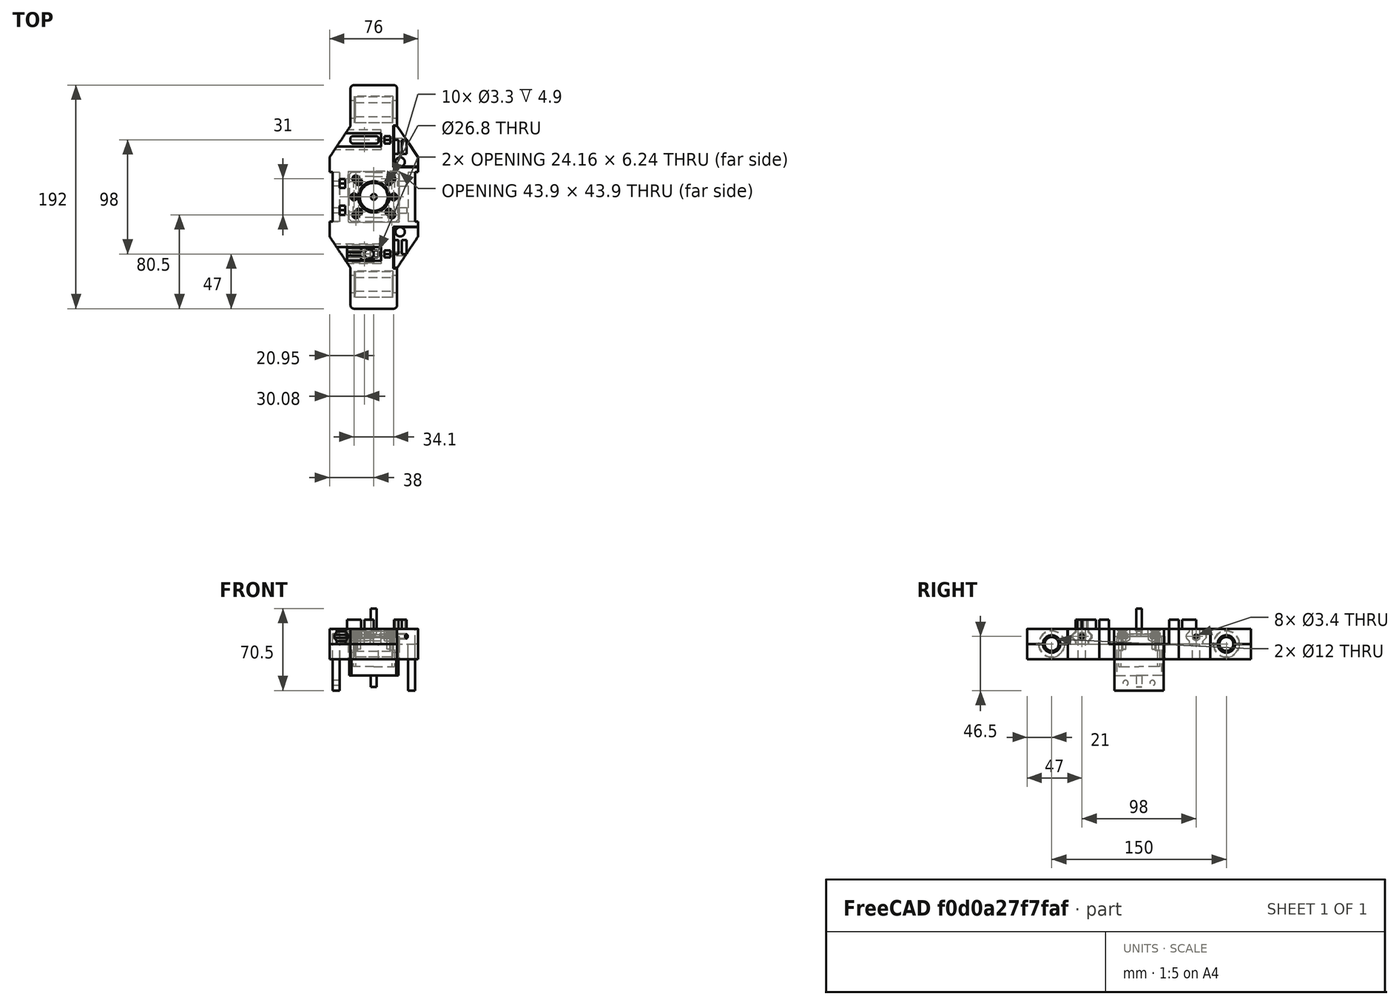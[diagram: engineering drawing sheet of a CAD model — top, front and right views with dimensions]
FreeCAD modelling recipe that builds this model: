
FCSTD DOCUMENT  (FreeCAD 0.16R6706 (Git))
Label: central_slider_v0
License: All rights reserved
LicenseURL: http://en.wikipedia.org/wiki/All_rights_reserved
objects: Part::Feature×19, Part::Cylinder×14, Part::FeaturePython×13, Part::MultiFuse×13, Part::Prism×10, Part::Extrusion×7, Part::Fuse×7, Part::Box×6, Part::Polygon×4, Part::Cut×4, Part::Circle×3, Part::Common×3, Part::Fillet×2
note: 105 computed .brp shape members not serialized (recipe doc carries the construction recipe); baked Part::Feature solids carry a one-line shape summary decoded from their .brp

FEATURE [Part::Polygon] topcenslid_box_sq
  Close = true
  Nodes = (4) [(-20,-96,0),(20,-96,0),(20,96,0),(-20,96,0)]
FEATURE [Part::Extrusion] topcenslid_box
  Base = -> topcenslid_box_sq
  Dir = (0,0,13)
  Solid = true
FEATURE [Part::Polygon] botcenslid_box_sq
  Close = true
  Nodes = (4) [(-20,-96,0),(20,-96,0),(20,96,0),(-20,96,0)]
FEATURE [Part::Extrusion] botcenslid_box
  Base = -> botcenslid_box_sq
  Dir = (0,0,13)
  Placement = pos=(0,0,-13) rot=(0,0,1;0rad)
  Solid = true
FEATURE [Part::Fillet] topcenslid_fllt
  Base = -> topcenslid_box
  Edges = 4 edges r=3: [Edge1,Edge2,Edge5,Edge8]
FEATURE [Part::Fillet] botcenslid_fllt
  Base = -> botcenslid_box
  Edges = 4 edges r=3: [Edge1,Edge2,Edge5,Edge8]
FEATURE [Part::Feature] topcenslidedent
  shape: bbox 76 x 125 x 13 mm, 14 faces (baked)
FEATURE [Part::Feature] botcenslidedent
  shape: bbox 76 x 125 x 13 mm, 14 faces (baked)
FEATURE [Part::Fuse] topcenslid_dent
  Base = -> topcenslid_fllt
  Tool = -> topcenslidedent
FEATURE [Part::Fuse] botcenslid_dent
  Base = -> botcenslid_fllt
  Tool = -> botcenslidedent
FEATURE [Part::Circle] toprod_circ
  Angle0 = 0
  Angle1 = 360
  Placement = pos=(-21,0,0) rot=(0,1,0;1.5708rad)
  Radius = 7.5
FEATURE [Part::Extrusion] toprod
  Base = -> toprod_circ
  Dir = (42,0,0)
  Placement = pos=(0,75,0) rot=(0,0,1;0rad)
  Solid = true
FEATURE [Part::Circle] botrod_circ
  Angle0 = 0
  Angle1 = 360
  Placement = pos=(-21,0,0) rot=(0,1,0;1.5708rad)
  Radius = 7.5
FEATURE [Part::Extrusion] botrod
  Base = -> botrod_circ
  Dir = (42,0,0)
  Placement = pos=(0,-75,0) rot=(0,0,1;0rad)
  Solid = true
FEATURE [Part::Feature] fbclt
  Placement = pos=(0,0,-0.1) rot=(0,0,1;0rad)
  shape: bbox 20.8 x 35 x 21 mm, 20 faces (baked)
FEATURE [Part::Feature] cbs_cfbclt
  shape: bbox 22.2 x 35.8 x 15 mm, 6 faces (baked)
FEATURE [Part::Feature] fbclb
  Placement = pos=(0,0,-0.2) rot=(0,0,1;0rad)
  shape: bbox 20.8 x 35 x 21 mm, 20 faces (baked)
FEATURE [Part::Feature] cbs_cfbclb
  shape: bbox 22.2 x 35.8 x 15 mm, 6 faces (baked)
FEATURE [Part::Cylinder] cen_lm12uu_0_ext
  Angle = 360
  Height = 32
  Placement = pos=(-16,0,0) rot=(0,1,0;1.5708rad)
  Radius = 11
FEATURE [Part::Cylinder] cen_lm12uu_0_int
  Angle = 360
  Height = 34
  Placement = pos=(-17,0,0) rot=(0,1,0;1.5708rad)
  Radius = 6
FEATURE [Part::Cut] cen_lm12uu_0
  Base = -> cen_lm12uu_0_ext
  Placement = pos=(0,75,0) rot=(0,0,1;0rad)
  Tool = -> cen_lm12uu_0_int
FEATURE [Part::Circle] cen_lm12uu_0_cont_circ
  Angle0 = 0
  Angle1 = 360
  Placement = pos=(-16.5,0,0) rot=(0,1,0;1.5708rad)
  Radius = 11.35
FEATURE [Part::Extrusion] cen_lm12uu_0_cont
  Base = -> cen_lm12uu_0_cont_circ
  Dir = (33,0,0)
  Placement = pos=(0,75,0) rot=(0,0,1;0rad)
  Solid = true
FEATURE [Part::FeaturePython] Clone  label="cen_lm12uu_001"  # Draft clone (typed FeaturePython)
  Objects = -> [cen_lm12uu_0]
  Placement = pos=(0,-75,0) rot=(0,0,1;0rad)
  Scale = (1,1,1)
FEATURE [Part::FeaturePython] Clone001  label="cen_lm12uu_0_cont001"  # Draft clone (typed FeaturePython)
  Objects = -> [cen_lm12uu_0_cont]
  Placement = pos=(0,-75,0) rot=(0,0,1;0rad)
  Scale = (1,1,1)
FEATURE [Part::Box] bclten0_cb1
  Height = 9
  Length = 12
  Placement = pos=(11,2.70833,12) rot=(0,0,1;0rad)
  Width = 4
FEATURE [Part::Box] bclten0_cb3
  Height = 9
  Length = 12
  Placement = pos=(11,9.50833,12) rot=(0,0,1;0rad)
  Width = 4
FEATURE [Part::Cylinder] bclten0_cyl
  Angle = 360
  Height = 9
  Placement = pos=(4,8.10833,12) rot=(0,0,1;0rad)
  Radius = 4
FEATURE [Part::Polygon] bclten0base_plane_yz
  Close = true
  Nodes = (12) [(0,2.90833,0),(0,2.90833,2.8375),(0,0.2,5.54583),(0,0.2,7.45417),(0,2.90833,10.1625),(0,2.90833,13),(0,13.3083,13),(0,13.3083,10.1625),+4 more]
FEATURE [Part::Extrusion] bclten0extr_base
  Base = -> bclten0base_plane_yz
  Dir = (23,0,0)
  Solid = true
FEATURE [Part::MultiFuse] bclten0clamp_base
  Shapes = -> [bclten0_cb1,bclten0_cb3,bclten0_cyl,bclten0extr_base]
FEATURE [Part::Polygon] bclten0_baseof_plane_yz
  Close = true
  Nodes = (12) [(0,2.30833,0),(0,2.30833,2.4375),(0,-0.4,5.14583),(0,-0.4,7.85417),(0,2.30833,10.5625),(0,2.30833,13),(0,13.9083,13),(0,13.9083,10.5625),+4 more]
FEATURE [Part::Extrusion] bclten0_baseof
  Base = -> bclten0_baseof_plane_yz
  Dir = (44.16,0,0)
  Placement = pos=(6.16,57.1083,0) rot=(0,0,1;3.14159rad)
  Solid = true
FEATURE [Part::Cylinder] bclten0_base_lscrew_shank
  Angle = 360
  Height = 25
  Placement = pos=(0,0,-1) rot=(0,0,1;0rad)
  Radius = 1.7
FEATURE [Part::Cylinder] bclten0_base_lscrew_head
  Angle = 360
  Height = 9.5
  Placement = pos=(0,0,-1) rot=(0,0,1;0rad)
  Radius = 2.95
FEATURE [Part::MultiFuse] bclten0_base_lscrew
  Placement = pos=(23,8.10833,6.5) rot=(0,-1,0;1.5708rad)
  Shapes = -> [bclten0_base_lscrew_shank,bclten0_base_lscrew_head]
FEATURE [Part::Prism] bclten0_base_lscrew_nut
  Circumradius = 3.605
  Height = 5.04
  Placement = pos=(3,8.10833,6.9) rot=(0,1,0;1.5708rad)
  Polygon = 6
FEATURE [Part::Box] bclten0_base_lscrew_nut2
  Height = 6.9
  Length = 5.04
  Placement = pos=(3,4.9864,0) rot=(0,0,1;0rad)
  Width = 6.24386
FEATURE [Part::MultiFuse] bclten0_clamp_hole
  Shapes = -> [bclten0_base_lscrew,bclten0_base_lscrew_nut,bclten0_base_lscrew_nut2]
FEATURE [Part::Cut] bclten0
  Base = -> bclten0clamp_base
  Placement = pos=(6.16,57.1083,0) rot=(0,0,1;3.14159rad)
  Tool = -> bclten0_clamp_hole
FEATURE [Part::Prism] bccr_nuthole0_nut
  Circumradius = 3.605
  Height = 5.04
  Placement = pos=(0,0,0) rot=(0,1,0;1.5708rad)
  Polygon = 6
FEATURE [Part::Box] bccr_nuthole0_hole
  Height = 7.9
  Length = 5.04
  Placement = pos=(0,-3.12193,0) rot=(0,0,1;0rad)
  Width = 6.24386
FEATURE [Part::Fuse] bccr_nuthole0
  Base = -> bccr_nuthole0_nut
  Placement = pos=(9.16,49,6.5) rot=(0,0,1;0rad)
  Tool = -> bccr_nuthole0_hole
FEATURE [Part::Feature] bcl_leads0
  shape: bbox 32.84 x 3.4 x 3.4 mm, 3 faces (baked)
FEATURE [Part::Feature] boxb0
  shape: bbox 24.16 x 6.244 x 15 mm, 10 faces (baked)
FEATURE [Part::MultiFuse] beltholes_t
  Shapes = -> [bccr_nuthole0,bclten0_baseof,bcl_leads0,boxb0]
FEATURE [Part::FeaturePython] Clone002  label="bclten1"  # Draft clone (typed FeaturePython)
  Objects = -> [bclten0]
  Placement = pos=(0,-40.8917,0) rot=(0,0,1;3.14159rad)
  Scale = (1,1,1)
FEATURE [Part::FeaturePython] Clone003  label="beltholes_b"  # Draft clone (typed FeaturePython)
  Objects = -> [beltholes_t]
  Placement = pos=(0,-98,0) rot=(0,0,1;0rad)
  Scale = (1,1,1)
FEATURE [Part::Cylinder] b2hole00_shank
  Angle = 360
  Height = 14
  Placement = pos=(0,0,-1) rot=(0,0,1;0rad)
  Radius = 1.65
FEATURE [Part::Cylinder] b2hole00_head
  Angle = 360
  Height = 4.3
  Placement = pos=(0,0,8.7) rot=(0,0,1;0rad)
  Radius = 2.9
FEATURE [Part::Prism] b2hole00_sup1
  Circumradius = 3.3
  Height = 3.6
  Placement = pos=(0,0,8.4) rot=(0,0,1;0.523599rad)
  Polygon = 3
FEATURE [Part::Cylinder] b2hole00_sup1away
  Angle = 360
  Height = 3.6
  Placement = pos=(0,0,8.4) rot=(0,0,1;0rad)
  Radius = 2.9
FEATURE [Part::Common] sup1cut
  Base = -> b2hole00_sup1
  Tool = -> b2hole00_sup1away
FEATURE [Part::Prism] b2hole00_sup2
  Circumradius = 1.8975
  Height = 3.9
  Placement = pos=(0,0,8.1) rot=(0,0,1;0rad)
  Polygon = 6
FEATURE [Part::MultiFuse] b2hole00
  Placement = pos=(-13,-13,-3.5) rot=(0,0,1;0rad)
  Shapes = -> [b2hole00_shank,b2hole00_head,sup1cut,b2hole00_sup2]
FEATURE [Part::FeaturePython] Clone004  label="b2hole01"  # Draft clone (typed FeaturePython)
  Objects = -> [b2hole00]
  Placement = pos=(-13,13,-3.5) rot=(0,0,1;0rad)
  Scale = (1,1,1)
FEATURE [Part::FeaturePython] Clone005  label="b2hole10"  # Draft clone (typed FeaturePython)
  Objects = -> [b2hole00]
  Placement = pos=(13,-13,-3.5) rot=(0,0,1;0rad)
  Scale = (1,1,1)
FEATURE [Part::FeaturePython] Clone006  label="b2hole11"  # Draft clone (typed FeaturePython)
  Objects = -> [b2hole00]
  Placement = pos=(13,13,-3.5) rot=(0,0,1;0rad)
  Scale = (1,1,1)
FEATURE [Part::MultiFuse] b2holes
  Shapes = -> [b2hole00,Clone004,Clone005,Clone006]
FEATURE [Part::Feature] nema14_my5602
  shape: bbox 35.2 x 35.2 x 50 mm, 26 faces (baked)
FEATURE [Part::Cylinder] b2hole00_shank001
  Angle = 360
  Height = 15
  Placement = pos=(0,0,-1) rot=(0,0,1;0rad)
  Radius = 1.65
FEATURE [Part::Cylinder] b2hole00_head001
  Angle = 360
  Height = 4.3
  Placement = pos=(0,0,9.7) rot=(0,0,1;0rad)
  Radius = 2.9
FEATURE [Part::Prism] b2hole00_sup1001
  Circumradius = 3.3
  Height = 3.6
  Placement = pos=(0,0,9.4) rot=(0,0,1;0.523599rad)
  Polygon = 3
FEATURE [Part::Cylinder] b2hole00_sup1away001
  Angle = 360
  Height = 3.6
  Placement = pos=(0,0,9.4) rot=(0,0,1;0rad)
  Radius = 2.9
FEATURE [Part::Common] sup1cut001
  Base = -> b2hole00_sup1001
  Tool = -> b2hole00_sup1away001
FEATURE [Part::Prism] b2hole00_sup2001
  Circumradius = 1.8975
  Height = 3.9
  Placement = pos=(0,0,9.1) rot=(0,0,1;0rad)
  Polygon = 6
FEATURE [Part::MultiFuse] b2hole00001
  Placement = pos=(-15.5,-15.5,-4.5) rot=(0,0,1;0rad)
  Shapes = -> [b2hole00_shank001,b2hole00_head001,sup1cut001,b2hole00_sup2001]
FEATURE [Part::FeaturePython] Clone007  label="b2hole00002"  # Draft clone (typed FeaturePython)
  Objects = -> [b2hole00001]
  Placement = pos=(-15.5,15.5,-4.5) rot=(0,0,1;0rad)
  Scale = (1,1,1)
FEATURE [Part::FeaturePython] Clone008  label="b2hole00003"  # Draft clone (typed FeaturePython)
  Objects = -> [b2hole00001]
  Placement = pos=(15.5,-15.5,-4.5) rot=(0,0,1;0rad)
  Scale = (1,1,1)
FEATURE [Part::FeaturePython] Clone009  label="b2hole00004"  # Draft clone (typed FeaturePython)
  Objects = -> [b2hole00001]
  Placement = pos=(15.5,15.5,-4.5) rot=(0,0,1;0rad)
  Scale = (1,1,1)
FEATURE [Part::MultiFuse] b2holes001
  Shapes = -> [b2hole00001,Clone007,Clone008,Clone009]
FEATURE [Part::Feature] nema17_ST4209S1006B
  shape: bbox 42.3 x 42.3 x 67.5 mm, 28 faces (baked)
FEATURE [Part::Feature] contmotors
  shape: bbox 43.9 x 43.9 x 67.5 mm, 296 faces (baked)
FEATURE [Part::Cylinder] bhole_notorstf0_shank
  Angle = 360
  Height = 10.5
  Placement = pos=(0,0,-1) rot=(0,0,1;0rad)
  Radius = 1.65
FEATURE [Part::Cylinder] bhole_notorstf0_head
  Angle = 360
  Height = 4.3
  Placement = pos=(0,0,5.2) rot=(0,0,1;0rad)
  Radius = 2.9
FEATURE [Part::Prism] bhole_notorstf0_sup1
  Circumradius = 3.3
  Height = 3.6
  Placement = pos=(0,0,4.9) rot=(0,0,1;0.523599rad)
  Polygon = 3
FEATURE [Part::Cylinder] bhole_notorstf0_sup1away
  Angle = 360
  Height = 3.6
  Placement = pos=(0,0,4.9) rot=(0,0,1;0rad)
  Radius = 2.9
FEATURE [Part::Common] sup1cut002
  Base = -> bhole_notorstf0_sup1
  Tool = -> bhole_notorstf0_sup1away
FEATURE [Part::Prism] bhole_notorstf0_sup2
  Circumradius = 1.8975
  Height = 3.9
  Placement = pos=(0,0,4.6) rot=(0,0,1;0rad)
  Polygon = 6
FEATURE [Part::MultiFuse] bhole_notorstf0
  Placement = pos=(-17.05,0,6.5) rot=(0,0,1;0rad)
  Shapes = -> [bhole_notorstf0_shank,bhole_notorstf0_head,sup1cut002,bhole_notorstf0_sup2]
FEATURE [Part::FeaturePython] Clone010  label="bhole_notorstf1"  # Draft clone (typed FeaturePython)
  Objects = -> [bhole_notorstf0]
  Placement = pos=(17.05,0,6.5) rot=(0,0,1;0rad)
  Scale = (1,1,1)
FEATURE [Part::Fuse] bholes_motorstf
  Base = -> bhole_notorstf0
  Tool = -> Clone010
FEATURE [Part::Feature] lg_hole_nx
  shape: bbox 3.6 x 42.6 x 28 mm, 6 faces (baked)
FEATURE [Part::Feature] lg_nx_sup
  shape: bbox 6 x 42 x 41 mm, 6 faces (baked)
FEATURE [Part::Prism] lg_nx_nuthole0_nut
  Circumradius = 4.43
  Height = 4.8
  Placement = pos=(0,0,0) rot=(0,1,0;1.5708rad)
  Polygon = 6
FEATURE [Part::Box] lg_nx_nuthole0_hole
  Height = 8.3
  Length = 4.8
  Placement = pos=(0,-3.83638,0) rot=(0,0,1;0rad)
  Width = 7.67276
FEATURE [Part::Fuse] lg_nx_nuthole0
  Base = -> lg_nx_nuthole0_nut
  Placement = pos=(-29.4,-11.5,6.1) rot=(0,0,1;0rad)
  Tool = -> lg_nx_nuthole0_hole
FEATURE [Part::FeaturePython] Clone011  label="lgnx_nuthole1"  # Draft clone (typed FeaturePython)
  Objects = -> [lg_nx_nuthole0]
  Placement = pos=(-29.4,11.5,6.1) rot=(0,0,1;0rad)
  Scale = (1,1,1)
FEATURE [Part::Feature] lg__nx_bolts
  shape: bbox 8 x 27.5 x 44.5 mm, 12 faces, 4 solids (baked)
FEATURE [Part::Feature] lg_nx_sup_hole
  shape: bbox 6.4 x 42.6 x 15 mm, 6 faces (baked)
FEATURE [Part::Feature] lg_hole_x
  shape: bbox 3.6 x 42.6 x 28 mm, 6 faces (baked)
FEATURE [Part::Feature] lg_x_sup
  shape: bbox 6 x 42 x 41 mm, 6 faces (baked)
FEATURE [Part::Prism] lg_x_nuthole0_nut
  Circumradius = 4.43
  Height = 4.8
  Placement = pos=(0,0,0) rot=(0,1,0;1.5708rad)
  Polygon = 6
FEATURE [Part::Box] lg_x_nuthole0_hole
  Height = 8.3
  Length = 4.8
  Placement = pos=(0,-3.83638,0) rot=(0,0,1;0rad)
  Width = 7.67276
FEATURE [Part::Fuse] lg_x_nuthole0
  Base = -> lg_x_nuthole0_nut
  Placement = pos=(35.4,-11.5,6.1) rot=(0,0,1;0rad)
  Tool = -> lg_x_nuthole0_hole
FEATURE [Part::FeaturePython] Clone012  label="lgx_nuthole1"  # Draft clone (typed FeaturePython)
  Objects = -> [lg_x_nuthole0]
  Placement = pos=(35.4,11.5,6.1) rot=(0,0,1;0rad)
  Scale = (1,1,1)
FEATURE [Part::Feature] lg_x_bolts
  shape: bbox 8 x 27.5 x 44.5 mm, 12 faces, 4 solids (baked)
FEATURE [Part::Feature] lg_x_sup_hole
  shape: bbox 6.4 x 42.6 x 15 mm, 6 faces (baked)
FEATURE [Part::MultiFuse] censlid_topholes
  Shapes = -> [toprod,botrod,cen_lm12uu_0_cont,Clone001,beltholes_t,Clone003,contmotors,bholes_motorstf,lg_hole_nx,lg_hole_x,cbs_cfbclt,cbs_cfbclb,lg_nx_nuthole0,Clone011,lg__nx_bolts,lg_x_nuthole0,Clone012,lg_x_bolts]
FEATURE [Part::MultiFuse] censlid_botholes
  Shapes = -> [toprod,botrod,cen_lm12uu_0_cont,Clone001,beltholes_t,Clone003,contmotors,bholes_motorstf,lg_hole_nx,lg_hole_x,lg_nx_sup_hole,lg_x_sup_hole]
FEATURE [Part::Fuse] central_slider_bear
  Base = -> cen_lm12uu_0
  Tool = -> Clone
FEATURE [Part::MultiFuse] central_slider_bot_sup
  Shapes = -> [topcenslid_dent,lg_nx_sup,lg_x_sup]
FEATURE [Part::MultiFuse] central_slider_bot_cl
  Shapes = -> [botcenslid_dent,fbclt,fbclb]
FEATURE [Part::Cut] central_slider_top
  Base = -> central_slider_bot_sup
  Tool = -> censlid_topholes
FEATURE [Part::Cut] central_slider_bot
  Base = -> central_slider_bot_cl
  Tool = -> censlid_botholes
